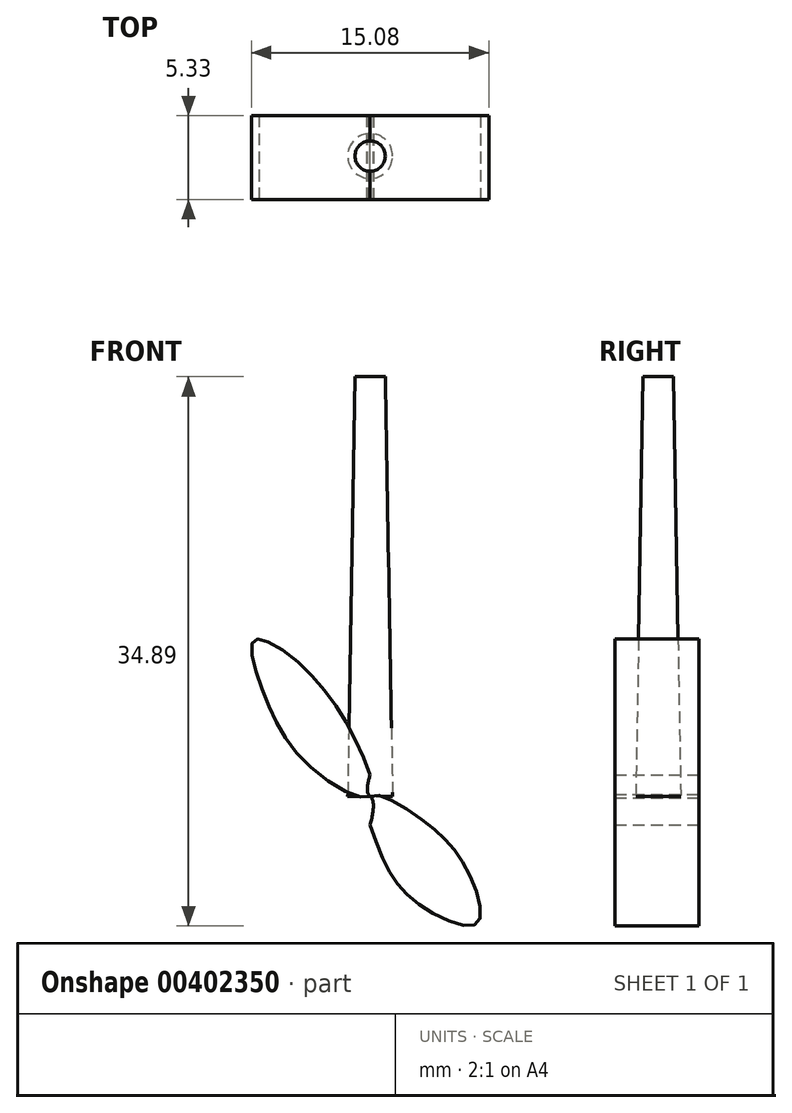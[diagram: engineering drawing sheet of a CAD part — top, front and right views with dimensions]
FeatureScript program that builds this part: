
annotation { "Feature Type Name" : "Feature", "Feature Type Description" : "" }
export const myFeature = defineFeature(function(context is Context, id is Id, definition is map)
    precondition{}
    {
        {
            var Q0;
            Q0=qCreatedBy(makeId("Front.planeOp"),FACE);
            var sketch = newSketch(context, id + "F0", { "sketchPlane" : qUnion([Q0])});
            skFitSpline(sketch, "E0", {"points": [v(0, 0) * mm, v(-0.83, 3.35) * mm, v(-4.28, 8.26) * mm, v(-7.37, 9.94) * mm, v(-6.85, 6.8) * mm, v(-4.02, 2.1) * mm, v(0, 0) * mm]});
            skFitSpline(sketch, "E1.MirrorC", {"points": [v(0, 0) * mm, v(0.83, 3.35) * mm, v(4.28, 8.26) * mm, v(7.37, 9.94) * mm, v(6.85, 6.8) * mm, v(4.02, 2.1) * mm, v(0, 0) * mm]});
            skSolve(sketch);
        }
        {
            var Q0;
            Q0=qCreatedBy(makeId("Front.planeOp"),FACE);
            var sketch = newSketch(context, id + "F1", { "sketchPlane" : qUnion([Q0])});
            skFitSpline(sketch, "E2", {"points": [v(0, 0) * mm, v(-3.44, -1.59) * mm, v(-6.17, -4.7) * mm, v(-6.8, -8.06) * mm, v(-3.25, -6.97) * mm, v(-0.67, -3.64) * mm, v(0, 0) * mm]});
            skFitSpline(sketch, "E3.MirrorC", {"points": [v(0, 0) * mm, v(3.44, -1.59) * mm, v(6.17, -4.7) * mm, v(6.8, -8.06) * mm, v(3.25, -6.97) * mm, v(0.67, -3.64) * mm, v(0, 0) * mm]});
            skSolve(sketch);
        }
        {
            var Q0;
            {var subQ0=sQuery(id+"F0.wireOp",EDGE,"E1.MirrorC");var subQ1=sQuery(id+"F0.wireOp",EDGE,"E0");var subQ2=makeQuery(id+"F0.imprint","INTERSECT",VERTEX,{"disambiguationData":[OD(0.0)],"derivedFrom":[subQ1,subQ0]});Q0=makeQuery(id+"F0.imprint","IMPRINT",FACE,{"disambiguationData":[TD([[makeQuery(id+"F0.imprint","IMPRINT",EDGE,{"disambiguationData":[TD([[subQ2,-1.0]])],"derivedFrom":subQ1}),-1.0]])]});}
            var Q1;
            {var subQ0=sQuery(id+"F0.wireOp",EDGE,"E1.MirrorC");var subQ1=sQuery(id+"F0.wireOp",EDGE,"E0");var subQ2=makeQuery(id+"F0.imprint","INTERSECT",VERTEX,{"disambiguationData":[OD(0.0)],"derivedFrom":[subQ1,subQ0]});Q1=makeQuery(id+"F0.imprint","IMPRINT",FACE,{"disambiguationData":[TD([[makeQuery(id+"F0.imprint","IMPRINT",EDGE,{"disambiguationData":[TD([[subQ2,1.0]])],"derivedFrom":subQ1}),1.0]])]});}
            var Q2;
            {var subQ0=sQuery(id+"F1.wireOp",EDGE,"E3.MirrorC");var subQ1=sQuery(id+"F1.wireOp",EDGE,"E2");var subQ2=makeQuery(id+"F1.imprint","INTERSECT",VERTEX,{"disambiguationData":[OD(0.0)],"derivedFrom":[subQ1,subQ0]});Q2=makeQuery(id+"F1.imprint","IMPRINT",FACE,{"disambiguationData":[TD([[makeQuery(id+"F1.imprint","IMPRINT",EDGE,{"disambiguationData":[TD([[subQ2,1.0]])],"derivedFrom":subQ1}),1.0]])]});}
            var Q3;
            {var subQ0=sQuery(id+"F1.wireOp",EDGE,"E3.MirrorC");var subQ1=sQuery(id+"F1.wireOp",EDGE,"E2");var subQ2=makeQuery(id+"F1.imprint","INTERSECT",VERTEX,{"disambiguationData":[OD(0.0)],"derivedFrom":[subQ1,subQ0]});Q3=makeQuery(id+"F1.imprint","IMPRINT",FACE,{"disambiguationData":[TD([[makeQuery(id+"F1.imprint","IMPRINT",EDGE,{"disambiguationData":[TD([[subQ2,-1.0]])],"derivedFrom":subQ1}),-1.0]])]});}
            extrude(context, id + "F2", {"entities" : qUnion([Q0, Q1, Q2, Q3]), "depth" : 5.33 * mm});
        }
        {
            var Q0;
            Q0=qCreatedBy(makeId("Top.planeOp"),FACE);
            var sketch = newSketch(context, id + "F3", { "sketchPlane" : qUnion([Q0])});
            skCircle(sketch, "E4", {"center": v(0, -2.57) * mm, "radius": 1.43 * mm});
            skSolve(sketch);
        }
        {
            var Q0;
            Q0 = qSketchRegion(id + "F3", true);
            extrude(context, id + "F4", {"entities" : qUnion([Q0]), "depth" : 26.67 * mm, "hasDraft" : true, "draftAngle" : 1 * degree, "draftPullDirection" : true});
        }
    });
